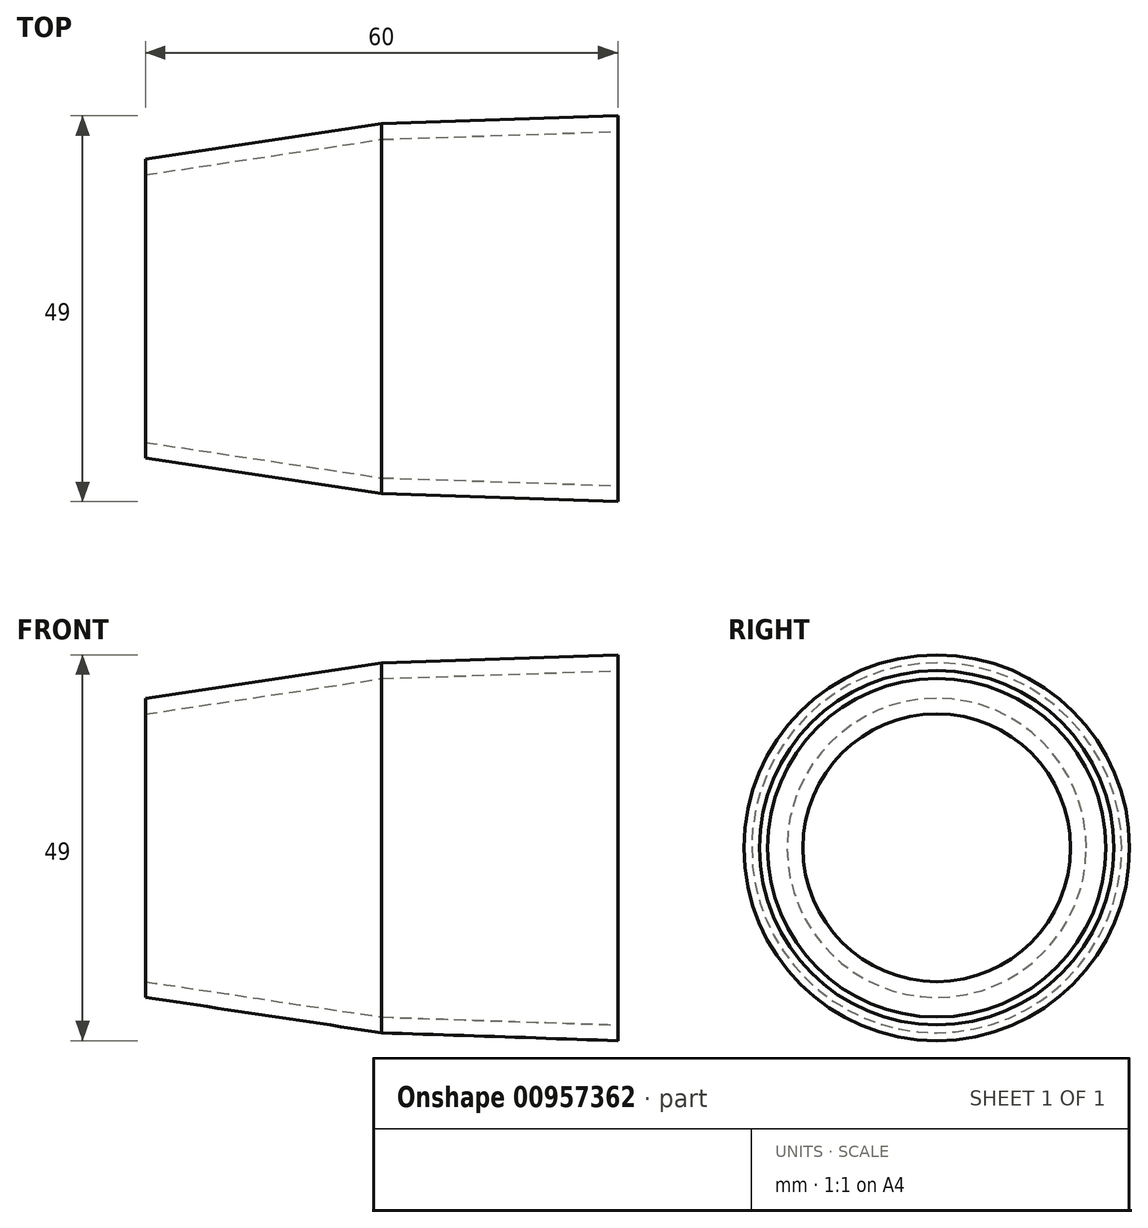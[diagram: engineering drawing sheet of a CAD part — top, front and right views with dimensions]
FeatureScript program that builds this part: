
annotation { "Feature Type Name" : "Feature", "Feature Type Description" : "" }
export const myFeature = defineFeature(function(context is Context, id is Id, definition is map)
    precondition{}
    {
        {
            var Q0;
            Q0=qCreatedBy(makeId("Top.planeOp"),FACE);
            var sketch = newSketch(context, id + "F0", { "sketchPlane" : qUnion([Q0])});
            skLineSegment(sketch, "E0", {"start": v(48.2, 24.5) * mm, "end": v(48.2, 22.5) * mm});
            skPoint(sketch, "E1", {"position": v(48.2, 22.5) * mm});
            skLineSegment(sketch, "E2", {"start": v(48.2, 22.5) * mm, "end": v(48.2, 0) * mm, "construction": true});
            skLineSegment(sketch, "E3", {"start": v(48.2, 0) * mm, "end": v(-11.8, 0) * mm, "construction": true});
            skLineSegment(sketch, "E4", {"start": v(-11.8, 0) * mm, "end": v(-11.8, 17) * mm, "construction": true});
            skLineSegment(sketch, "E5", {"start": v(18.2, 0) * mm, "end": v(18.2, 21.5) * mm, "construction": true});
            skLineSegment(sketch, "E6", {"start": v(48.2, 22.5) * mm, "end": v(18.2, 21.5) * mm});
            skLineSegment(sketch, "E7", {"start": v(18.2, 21.5) * mm, "end": v(-11.8, 17) * mm});
            skLineSegment(sketch, "E8", {"start": v(-11.8, 17) * mm, "end": v(-11.8, 19) * mm});
            skLineSegment(sketch, "E9", {"start": v(-11.8, 19) * mm, "end": v(18.2, 23.5) * mm});
            skLineSegment(sketch, "E10", {"start": v(18.2, 23.5) * mm, "end": v(48.2, 24.5) * mm});
            skSolve(sketch);
        }
        {
            var Q0;
            Q0 = qSketchRegion(id + "F0", true);
            var Q1;
            Q1=sQuery(id+"F0.wireOp",EDGE,"E3");
            revolve(context, id + "F1", {"surfaceOperationType" : NewSurfaceOperationType.NEW, "entities" : qUnion([Q0]), "axis" : qUnion([Q1]), "revolveType" : RevolveType.FULL});
        }
    });
